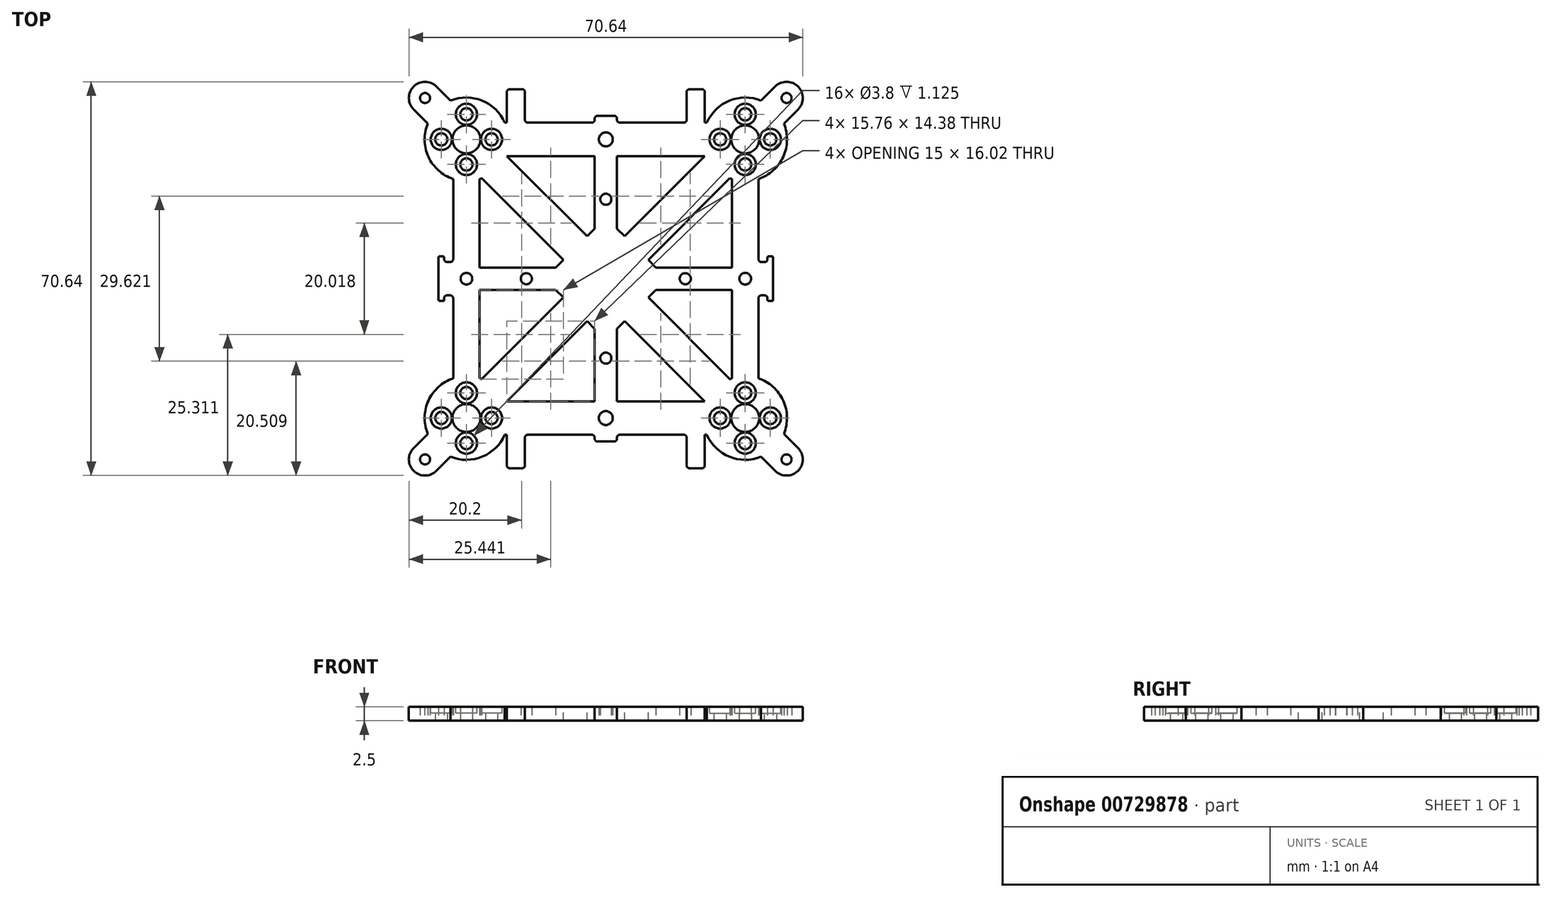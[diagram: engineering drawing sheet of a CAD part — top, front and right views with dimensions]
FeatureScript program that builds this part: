
annotation { "Feature Type Name" : "Feature", "Feature Type Description" : "" }
export const myFeature = defineFeature(function(context is Context, id is Id, definition is map)
    precondition{}
    {
        {
            var Q0;
            Q0=qCreatedBy(makeId("Top.planeOp"),FACE);
            var sketch = newSketch(context, id + "F0", { "sketchPlane" : qUnion([Q0])});
            skLineSegment(sketch, "E0", {"start": v(0, 0) * mm, "end": v(-25, 0) * mm, "construction": true});
            skLineSegment(sketch, "E1", {"start": v(0, 0) * mm, "end": v(118.4, 0) * mm, "construction": true});
            skLineSegment(sketch, "E2", {"start": v(0, 0) * mm, "end": v(0, 58.74) * mm, "construction": true});
            skLineSegment(sketch, "E3", {"start": v(-25, 0) * mm, "end": v(-25, 62.06) * mm, "construction": true});
            skLineSegment(sketch, "E4", {"start": v(42.47, 25) * mm, "end": v(-80.33, 25) * mm, "construction": true});
            skLineSegment(sketch, "E5", {"start": v(0, 0) * mm, "end": v(-25, 25) * mm, "construction": true});
            skLineSegment(sketch, "E6", {"start": v(-25, 25) * mm, "end": v(-64.7, 64.7) * mm, "construction": true});
            skCircle(sketch, "E7", {"center": v(-25, 25) * mm, "radius": 7.5 * mm});
            skCircle(sketch, "E8", {"center": v(-25, 25) * mm, "radius": 2.5 * mm});
            skCircle(sketch, "E9", {"center": v(-25, 25) * mm, "radius": 4.5 * mm, "construction": true});
            skCircle(sketch, "E10", {"center": v(-25, 20.5) * mm, "radius": 1.1 * mm});
            skCircle(sketch, "E11", {"center": v(-20.5, 25) * mm, "radius": 1.1 * mm});
            skCircle(sketch, "E12.MirrorC", {"center": v(-25, 29.5) * mm, "radius": 1.1 * mm});
            skCircle(sketch, "E13.MirrorC", {"center": v(-29.5, 25) * mm, "radius": 1.1 * mm});
            skCircle(sketch, "E14", {"center": v(-32.42, 32.42) * mm, "radius": 0.9 * mm});
            skCircle(sketch, "E15.0", {"center": v(-32.42, 32.42) * mm, "radius": 2.9 * mm});
            skLineSegment(sketch, "E16", {"start": v(-30.37, 34.48) * mm, "end": v(-27.84, 31.94) * mm});
            skLineSegment(sketch, "E17.MirrorCS", {"start": v(-34.48, 30.37) * mm, "end": v(-31.94, 27.84) * mm});
            skArc(sketch, "E18", {"start": v(-23.95, 0) * mm, "mid": v(-25, 1.05) * mm, "end": v(-26.05, 0) * mm});
            skArc(sketch, "E19", {"start": v(-13.25, 0) * mm, "mid": v(-14.25, 1) * mm, "end": v(-15.25, 0) * mm});
            skLineSegment(sketch, "E20", {"start": v(-26.05, 0) * mm, "end": v(-30, 0) * mm});
            skLineSegment(sketch, "E21", {"start": v(-30, 0) * mm, "end": v(-30, 4) * mm});
            skLineSegment(sketch, "E22", {"start": v(-30, 4) * mm, "end": v(-29, 4) * mm});
            skLineSegment(sketch, "E23", {"start": v(-29, 4) * mm, "end": v(-29, 3) * mm});
            skArc(sketch, "E24", {"start": v(0, 26.25) * mm, "mid": v(-1.25, 25) * mm, "end": v(0, 23.75) * mm});
            skArc(sketch, "E25", {"start": v(0, 15.25) * mm, "mid": v(-1, 14.25) * mm, "end": v(0, 13.25) * mm});
            skLineSegment(sketch, "E26", {"start": v(-22.62, 2) * mm, "end": v(-2, 2) * mm});
            skLineSegment(sketch, "E27", {"start": v(-23.95, 0) * mm, "end": v(-15.25, 0) * mm});
            skLineSegment(sketch, "E28", {"start": v(-13.25, 0) * mm, "end": v(0, 0) * mm});
            skLineSegment(sketch, "E29.bottom", {"start": v(-2, 29.22) * mm, "end": v(0, 29.22) * mm});
            skLineSegment(sketch, "E29.left", {"start": v(-2, 29.22) * mm, "end": v(-2, 2) * mm});
            skPoint(sketch, "E29.middle", {"position": v(0, 0) * mm});
            skLineSegment(sketch, "E30", {"start": v(0, 29.22) * mm, "end": v(0, 26.25) * mm});
            skLineSegment(sketch, "E31.trimOffspring", {"start": v(-26.05, 0) * mm, "end": v(-94.42, 0) * mm, "construction": true});
            skLineSegment(sketch, "E32", {"start": v(0, 23.75) * mm, "end": v(0, 15.25) * mm});
            skLineSegment(sketch, "E33", {"start": v(0, 13.25) * mm, "end": v(0, 0) * mm});
            skLineSegment(sketch, "E34.left", {"start": v(-27.38, 17.89) * mm, "end": v(-27.38, 3) * mm});
            skLineSegment(sketch, "E34.right", {"start": v(-22.62, 17.89) * mm, "end": v(-22.62, 2) * mm});
            skLineSegment(sketch, "E35", {"start": v(-29, 3) * mm, "end": v(-27.38, 3) * mm});
            skPoint(sketch, "E36", {"position": v(-2, 9) * mm});
            skPoint(sketch, "E37", {"position": v(-9, 2) * mm});
            skLineSegment(sketch, "E38", {"start": v(-9, 2) * mm, "end": v(-2, 9) * mm});
            skPoint(sketch, "E39", {"position": v(-3.38, 7.62) * mm});
            skLineSegment(sketch, "E40", {"start": v(-3.38, 7.62) * mm, "end": v(-18.02, 22.26) * mm});
            skLineSegment(sketch, "E41.MirrorCS", {"start": v(-7.62, 3.38) * mm, "end": v(-22.26, 18.02) * mm});
            skPoint(sketch, "E42", {"position": v(-2, 22) * mm});
            skLineSegment(sketch, "E43", {"start": v(-2, 22) * mm, "end": v(-18.13, 22) * mm});
            skLineSegment(sketch, "E44.MirrorCS", {"start": v(-2, 28) * mm, "end": v(-18.13, 28) * mm});
            skLineSegment(sketch, "E45", {"start": v(-14.5, 28) * mm, "end": v(-14.5, 34) * mm});
            skLineSegment(sketch, "E46", {"start": v(-17.75, 28) * mm, "end": v(-17.75, 34) * mm});
            skLineSegment(sketch, "E47", {"start": v(-14.5, 34) * mm, "end": v(-17.75, 34) * mm});
            skSolve(sketch);
        }
        {
            var Q0;
            Q0 = qSketchRegion(id + "F0", true);
            var Q1;
            {var subQ1=sQuery(id+"F0.wireOp",EDGE,"E26");var subQ4=sQuery(id+"F0.wireOp",EDGE,"E29.left");var subQ5=makeQuery(id+"F0.imprint","INTERSECT",VERTEX,{"derivedFrom":[subQ1,subQ4]});Q1=makeQuery(id+"F0.imprint","IMPRINT",FACE,{"disambiguationData":[TD([[makeQuery(id+"F0.imprint","IMPRINT",EDGE,{"disambiguationData":[TD([[subQ5,1.0]])],"derivedFrom":subQ1}),1.0]])]});}
            extrude(context, id + "F1", {"entities" : qUnion([Q0, Q1]), "depth" : 2.5 * mm, "offsetDistance" : 25 * mm});
        }
        {
            var Q0;
            Q0=makeQuery(id+"F1.opExtrude","CAP_FACE",FACE,{"disambiguationData":[OSD([sQuery(id+"F0.wireOp",EDGE,"E7"),sQuery(id+"F0.wireOp",EDGE,"E8"),sQuery(id+"F0.wireOp",EDGE,"E10"),sQuery(id+"F0.wireOp",EDGE,"E11"),sQuery(id+"F0.wireOp",EDGE,"E12.MirrorC"),sQuery(id+"F0.wireOp",EDGE,"E13.MirrorC"),sQuery(id+"F0.wireOp",EDGE,"E14"),sQuery(id+"F0.wireOp",EDGE,"E15.0"),sQuery(id+"F0.wireOp",EDGE,"E16"),sQuery(id+"F0.wireOp",EDGE,"E17.MirrorCS"),sQuery(id+"F0.wireOp",EDGE,"E18"),sQuery(id+"F0.wireOp",EDGE,"E19"),sQuery(id+"F0.wireOp",EDGE,"E20"),sQuery(id+"F0.wireOp",EDGE,"E21"),sQuery(id+"F0.wireOp",EDGE,"E22"),sQuery(id+"F0.wireOp",EDGE,"E23"),sQuery(id+"F0.wireOp",EDGE,"E24"),sQuery(id+"F0.wireOp",EDGE,"E25"),sQuery(id+"F0.wireOp",EDGE,"E26"),sQuery(id+"F0.wireOp",EDGE,"E27"),sQuery(id+"F0.wireOp",EDGE,"E28"),sQuery(id+"F0.wireOp",EDGE,"E29.bottom"),sQuery(id+"F0.wireOp",EDGE,"E29.left"),sQuery(id+"F0.wireOp",EDGE,"E30"),sQuery(id+"F0.wireOp",EDGE,"E32"),sQuery(id+"F0.wireOp",EDGE,"E33"),sQuery(id+"F0.wireOp",EDGE,"E34.left"),sQuery(id+"F0.wireOp",EDGE,"E34.right"),sQuery(id+"F0.wireOp",EDGE,"E35"),sQuery(id+"F0.wireOp",EDGE,"E38"),sQuery(id+"F0.wireOp",EDGE,"E40"),sQuery(id+"F0.wireOp",EDGE,"E43"),sQuery(id+"F0.wireOp",EDGE,"E44.MirrorCS"),sQuery(id+"F0.wireOp",EDGE,"E45"),sQuery(id+"F0.wireOp",EDGE,"E46"),sQuery(id+"F0.wireOp",EDGE,"E47")])],"isStart":false});
            var sketch = newSketch(context, id + "F2", { "sketchPlane" : qUnion([Q0])});
            skCircle(sketch, "E48.0", {"center": v(-25, 29.5) * mm, "radius": 1.1 * mm});
            skCircle(sketch, "E48.1", {"center": v(-29.5, 25) * mm, "radius": 1.1 * mm});
            skCircle(sketch, "E48.2", {"center": v(-25, 20.5) * mm, "radius": 1.1 * mm});
            skCircle(sketch, "E48.3", {"center": v(-20.5, 25) * mm, "radius": 1.1 * mm});
            skCircle(sketch, "E49.0", {"center": v(-29.5, 25) * mm, "radius": 1.9 * mm});
            skCircle(sketch, "E50.0", {"center": v(-25, 29.5) * mm, "radius": 1.9 * mm});
            skCircle(sketch, "E51.0", {"center": v(-20.5, 25) * mm, "radius": 1.9 * mm});
            skCircle(sketch, "E52.0", {"center": v(-25, 20.5) * mm, "radius": 1.9 * mm});
            skSolve(sketch);
        }
        {
            var Q0;
            Q0 = qSketchRegion(id + "F2", true);
            extrude(context, id + "F3", {"entities" : qUnion([Q0]), "operationType" : NewBodyOperationType.REMOVE, "oppositeDirection" : true, "depth" : (2.25 / 2) * mm, "offsetDistance" : 25 * mm});
        }
        {
            var Q0;
            Q0=makeQuery(id+"F1.opExtrude","SWEPT_FACE",FACE,{"disambiguationData":[OSD([sQuery(id+"F0.wireOp",EDGE,"E38")])]});
            var sketch = newSketch(context, id + "F4", { "sketchPlane" : qUnion([Q0])});
            skLineSegment(sketch, "E53", {"start": v(0, 2.5) * mm, "end": v(0, -2.32) * mm, "construction": true});
            skPoint(sketch, "E53.endSnap0", {"position": v(0, 0) * mm});
            skPoint(sketch, "E54", {"position": v(-3, 0) * mm});
            skLineSegment(sketch, "E55", {"start": v(-3, 0) * mm, "end": v(-3, 2.5) * mm});
            skLineSegment(sketch, "E56.MirrorCS", {"start": v(3, 0) * mm, "end": v(3, 2.5) * mm});
            skSolve(sketch);
        }
        {
            var Q0;
            Q0 = qSketchRegion(id + "F4", true);
            var Q1;
            {var subQ0=sQuery(id+"F4.wireOp",EDGE,"E55");Q1=makeQuery(id+"F4.imprint","IMPRINT",FACE,{"disambiguationData":[TD([[makeQuery(id+"F4.imprint","IMPRINT",EDGE,{"derivedFrom":subQ0}),-1.0]])]});}
            extrude(context, id + "F5", {"entities" : qUnion([Q0, Q1]), "operationType" : NewBodyOperationType.ADD, "depth" : 21 * mm, "offsetDistance" : 25 * mm});
        }
        {
            var Q0;
            Q0=makeQuery(id+"F1.opExtrude","SWEPT_EDGE",EDGE,{"disambiguationData":[OSD([sQuery(id+"F0.wireOp",EDGE,"E34.left"),sQuery(id+"F0.wireOp",EDGE,"E35")])]});
            var Q1;
            Q1=makeQuery(id+"F1.opExtrude","SWEPT_EDGE",EDGE,{"disambiguationData":[OSD([sQuery(id+"F0.wireOp",EDGE,"E23"),sQuery(id+"F0.wireOp",EDGE,"E35")])]});
            var Q2;
            Q2=makeQuery(id+"F1.opExtrude","SWEPT_EDGE",EDGE,{"disambiguationData":[OSD([sQuery(id+"F0.wireOp",EDGE,"E44.MirrorCS"),sQuery(id+"F0.wireOp",EDGE,"E45")])]});
            var Q3;
            Q3=makeQuery(id+"F1.opExtrude","SWEPT_EDGE",EDGE,{"disambiguationData":[OSD([sQuery(id+"F0.wireOp",EDGE,"E45"),sQuery(id+"F0.wireOp",EDGE,"E47")])]});
            var Q4;
            Q4=makeQuery(id+"F1.opExtrude","SWEPT_EDGE",EDGE,{"disambiguationData":[OSD([sQuery(id+"F0.wireOp",EDGE,"E46"),sQuery(id+"F0.wireOp",EDGE,"E47")])]});
            var Q5;
            Q5=makeQuery(id+"F1.opExtrude","SWEPT_EDGE",EDGE,{"disambiguationData":[OSD([sQuery(id+"F0.wireOp",EDGE,"E29.bottom"),sQuery(id+"F0.wireOp",EDGE,"E29.left")])]});
            var Q6;
            Q6=makeQuery(id+"F1.opExtrude","SWEPT_EDGE",EDGE,{"disambiguationData":[OSD([sQuery(id+"F0.wireOp",EDGE,"E29.left"),sQuery(id+"F0.wireOp",EDGE,"E44.MirrorCS")])]});
            fillet(context, id + "F6", {"entities" : qUnion([Q0, Q1, Q2, Q3, Q4, Q5, Q6]), "radius" : 0.5 * mm, "tangentPropagation" : true, "allowEdgeOverflow" : false});
        }
        {
            var Q0;
            Q0=makeQuery(id+"F1.opExtrude","SWEPT_EDGE",EDGE,{"disambiguationData":[OSD([sQuery(id+"F0.wireOp",EDGE,"E21"),sQuery(id+"F0.wireOp",EDGE,"E22")])]});
            var Q1;
            Q1=makeQuery(id+"F1.opExtrude","SWEPT_EDGE",EDGE,{"disambiguationData":[OSD([sQuery(id+"F0.wireOp",EDGE,"E22"),sQuery(id+"F0.wireOp",EDGE,"E23")])]});
            fillet(context, id + "F7", {"entities" : qUnion([Q0, Q1]), "radius" : 0.2 * mm, "tangentPropagation" : true, "allowEdgeOverflow" : false});
        }
        {
            var Q0;
            Q0=makeQuery(id+"F1.opExtrude","SWEPT_BODY",BODY,{"disambiguationData":[OSD([sQuery(id+"F0.wireOp",EDGE,"E7"),sQuery(id+"F0.wireOp",EDGE,"E8"),sQuery(id+"F0.wireOp",EDGE,"E10"),sQuery(id+"F0.wireOp",EDGE,"E11"),sQuery(id+"F0.wireOp",EDGE,"E12.MirrorC"),sQuery(id+"F0.wireOp",EDGE,"E13.MirrorC"),sQuery(id+"F0.wireOp",EDGE,"E14"),sQuery(id+"F0.wireOp",EDGE,"E15.0"),sQuery(id+"F0.wireOp",EDGE,"E16"),sQuery(id+"F0.wireOp",EDGE,"E17.MirrorCS"),sQuery(id+"F0.wireOp",EDGE,"E18"),sQuery(id+"F0.wireOp",EDGE,"E19"),sQuery(id+"F0.wireOp",EDGE,"E20"),sQuery(id+"F0.wireOp",EDGE,"E21"),sQuery(id+"F0.wireOp",EDGE,"E22"),sQuery(id+"F0.wireOp",EDGE,"E23"),sQuery(id+"F0.wireOp",EDGE,"E24"),sQuery(id+"F0.wireOp",EDGE,"E25"),sQuery(id+"F0.wireOp",EDGE,"E26"),sQuery(id+"F0.wireOp",EDGE,"E27"),sQuery(id+"F0.wireOp",EDGE,"E28"),sQuery(id+"F0.wireOp",EDGE,"E29.bottom"),sQuery(id+"F0.wireOp",EDGE,"E29.left"),sQuery(id+"F0.wireOp",EDGE,"E30"),sQuery(id+"F0.wireOp",EDGE,"E32"),sQuery(id+"F0.wireOp",EDGE,"E33"),sQuery(id+"F0.wireOp",EDGE,"E34.left"),sQuery(id+"F0.wireOp",EDGE,"E34.right"),sQuery(id+"F0.wireOp",EDGE,"E35"),sQuery(id+"F0.wireOp",EDGE,"E38"),sQuery(id+"F0.wireOp",EDGE,"E40"),sQuery(id+"F0.wireOp",EDGE,"E43"),sQuery(id+"F0.wireOp",EDGE,"E44.MirrorCS")])]});
            var Q1;
            Q1=makeQuery(id+"F1.opExtrude","SWEPT_FACE",FACE,{"disambiguationData":[OSD([sQuery(id+"F0.wireOp",EDGE,"E28")])]});
            mirror(context, id + "F8", {"operationType" : NewBodyOperationType.ADD, "entities" : qUnion([Q0]), "mirrorPlane" : qUnion([Q1])});
        }
        {
            var Q0;
            Q0=makeQuery(id+"F1.opExtrude","SWEPT_BODY",BODY,{"disambiguationData":[OSD([sQuery(id+"F0.wireOp",EDGE,"E7"),sQuery(id+"F0.wireOp",EDGE,"E8"),sQuery(id+"F0.wireOp",EDGE,"E10"),sQuery(id+"F0.wireOp",EDGE,"E11"),sQuery(id+"F0.wireOp",EDGE,"E12.MirrorC"),sQuery(id+"F0.wireOp",EDGE,"E13.MirrorC"),sQuery(id+"F0.wireOp",EDGE,"E14"),sQuery(id+"F0.wireOp",EDGE,"E15.0"),sQuery(id+"F0.wireOp",EDGE,"E16"),sQuery(id+"F0.wireOp",EDGE,"E17.MirrorCS"),sQuery(id+"F0.wireOp",EDGE,"E18"),sQuery(id+"F0.wireOp",EDGE,"E19"),sQuery(id+"F0.wireOp",EDGE,"E20"),sQuery(id+"F0.wireOp",EDGE,"E21"),sQuery(id+"F0.wireOp",EDGE,"E22"),sQuery(id+"F0.wireOp",EDGE,"E23"),sQuery(id+"F0.wireOp",EDGE,"E24"),sQuery(id+"F0.wireOp",EDGE,"E25"),sQuery(id+"F0.wireOp",EDGE,"E26"),sQuery(id+"F0.wireOp",EDGE,"E27"),sQuery(id+"F0.wireOp",EDGE,"E28"),sQuery(id+"F0.wireOp",EDGE,"E29.bottom"),sQuery(id+"F0.wireOp",EDGE,"E29.left"),sQuery(id+"F0.wireOp",EDGE,"E30"),sQuery(id+"F0.wireOp",EDGE,"E32"),sQuery(id+"F0.wireOp",EDGE,"E33"),sQuery(id+"F0.wireOp",EDGE,"E34.left"),sQuery(id+"F0.wireOp",EDGE,"E34.right"),sQuery(id+"F0.wireOp",EDGE,"E35"),sQuery(id+"F0.wireOp",EDGE,"E38"),sQuery(id+"F0.wireOp",EDGE,"E40"),sQuery(id+"F0.wireOp",EDGE,"E43"),sQuery(id+"F0.wireOp",EDGE,"E44.MirrorCS")])]});
            var Q1;
            Q1=makeQuery(id+"F1.opExtrude","SWEPT_FACE",FACE,{"disambiguationData":[OSD([sQuery(id+"F0.wireOp",EDGE,"E32")])]});
            mirror(context, id + "F9", {"operationType" : NewBodyOperationType.ADD, "entities" : qUnion([Q0]), "mirrorPlane" : qUnion([Q1])});
        }
    });
